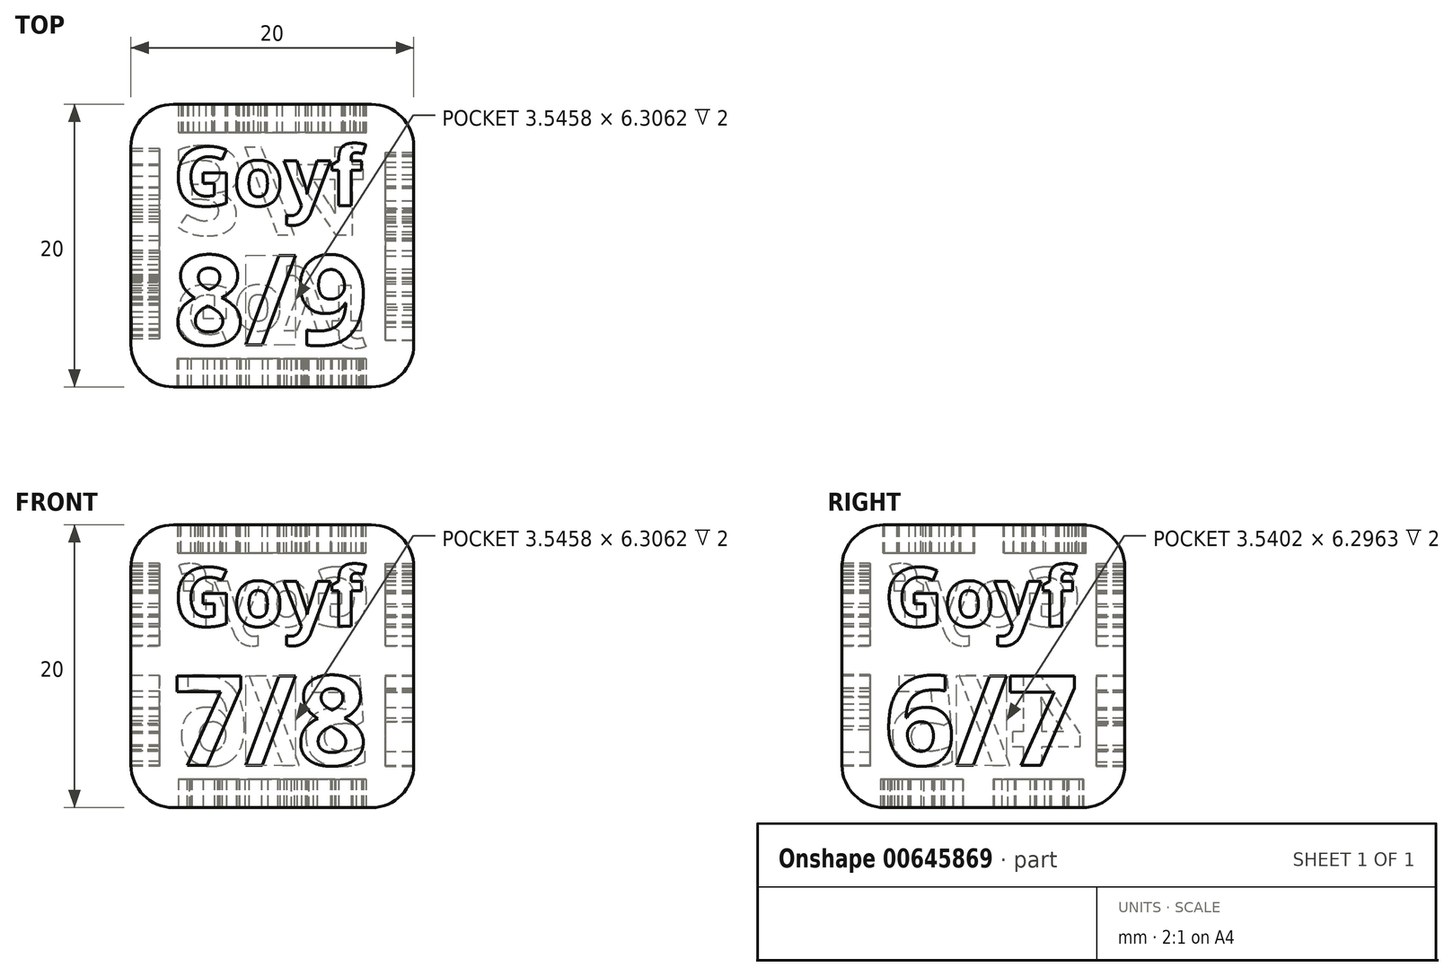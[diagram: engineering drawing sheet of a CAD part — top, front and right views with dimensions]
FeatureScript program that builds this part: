
annotation { "Feature Type Name" : "Feature", "Feature Type Description" : "" }
export const myFeature = defineFeature(function(context is Context, id is Id, definition is map)
    precondition{}
    {
        {
            var Q0;
            Q0=qCreatedBy(makeId("Top.planeOp"),FACE);
            var sketch = newSketch(context, id + "F0", { "sketchPlane" : qUnion([Q0])});
            skLineSegment(sketch, "E0.bottom", {"start": v(0, 0) * mm, "end": v(20, 0) * mm});
            skLineSegment(sketch, "E0.top", {"start": v(0, 20) * mm, "end": v(20, 20) * mm});
            skLineSegment(sketch, "E0.left", {"start": v(0, 0) * mm, "end": v(0, 20) * mm});
            skLineSegment(sketch, "E0.right", {"start": v(20, 0) * mm, "end": v(20, 20) * mm});
            skSolve(sketch);
        }
        {
            var Q0;
            Q0 = qSketchRegion(id + "F0", true);
            extrude(context, id + "F1", {"entities" : qUnion([Q0]), "depth" : 20 * mm, "offsetDistance" : 25 * mm});
        }
        {
            var Q0;
            Q0=makeQuery(id+"F1.opExtrude","CAP_EDGE",EDGE,{"disambiguationData":[OSD([sQuery(id+"F0.wireOp",EDGE,"E0.top")])],"isStart":true});
            var Q1;
            Q1=makeQuery(id+"F1.opExtrude","CAP_EDGE",EDGE,{"disambiguationData":[OSD([sQuery(id+"F0.wireOp",EDGE,"E0.left")])],"isStart":true});
            var Q2;
            Q2=makeQuery(id+"F1.opExtrude","SWEPT_EDGE",EDGE,{"disambiguationData":[OSD([sQuery(id+"F0.wireOp",EDGE,"E0.top"),sQuery(id+"F0.wireOp",EDGE,"E0.left")])]});
            var Q3;
            Q3=makeQuery(id+"F1.opExtrude","SWEPT_EDGE",EDGE,{"disambiguationData":[OSD([sQuery(id+"F0.wireOp",EDGE,"E0.top"),sQuery(id+"F0.wireOp",EDGE,"E0.right")])]});
            var Q4;
            Q4=makeQuery(id+"F1.opExtrude","SWEPT_FACE",FACE,{"disambiguationData":[OSD([sQuery(id+"F0.wireOp",EDGE,"E0.top")])]});
            var Q5;
            Q5=makeQuery(id+"F1.opExtrude","CAP_EDGE",EDGE,{"disambiguationData":[OSD([sQuery(id+"F0.wireOp",EDGE,"E0.right")])],"isStart":false});
            var Q6;
            Q6=makeQuery(id+"F1.opExtrude","CAP_EDGE",EDGE,{"disambiguationData":[OSD([sQuery(id+"F0.wireOp",EDGE,"E0.left")])],"isStart":false});
            var Q7;
            Q7=makeQuery(id+"F1.opExtrude","CAP_EDGE",EDGE,{"disambiguationData":[OSD([sQuery(id+"F0.wireOp",EDGE,"E0.bottom")])],"isStart":false});
            var Q8;
            Q8=makeQuery(id+"F1.opExtrude","SWEPT_EDGE",EDGE,{"disambiguationData":[OSD([sQuery(id+"F0.wireOp",EDGE,"E0.bottom"),sQuery(id+"F0.wireOp",EDGE,"E0.left")])]});
            var Q9;
            Q9=makeQuery(id+"F1.opExtrude","CAP_EDGE",EDGE,{"disambiguationData":[OSD([sQuery(id+"F0.wireOp",EDGE,"E0.bottom")])],"isStart":true});
            var Q10;
            Q10=makeQuery(id+"F1.opExtrude","SWEPT_EDGE",EDGE,{"disambiguationData":[OSD([sQuery(id+"F0.wireOp",EDGE,"E0.bottom"),sQuery(id+"F0.wireOp",EDGE,"E0.right")])]});
            var Q11;
            Q11=makeQuery(id+"F1.opExtrude","CAP_EDGE",EDGE,{"disambiguationData":[OSD([sQuery(id+"F0.wireOp",EDGE,"E0.right")])],"isStart":true});
            fillet(context, id + "F2", {"entities" : qUnion([Q0, Q1, Q2, Q3, Q4, Q5, Q6, Q7, Q8, Q9, Q10, Q11]), "radius" : 3 * mm, "tangentPropagation" : true, "allowEdgeOverflow" : false});
        }
        {
            var Q0;
            Q0=makeQuery(id+"F1.opExtrude","CAP_FACE",FACE,{"disambiguationData":[OSD([sQuery(id+"F0.wireOp",EDGE,"E0.bottom"),sQuery(id+"F0.wireOp",EDGE,"E0.top"),sQuery(id+"F0.wireOp",EDGE,"E0.left"),sQuery(id+"F0.wireOp",EDGE,"E0.right")])],"isStart":false});
            var sketch = newSketch(context, id + "F3", { "sketchPlane" : qUnion([Q0])});
            skText(sketch, "E1", { "text": "Goyf", "fontName": "OpenSans-Bold.ttf"});
            skText(sketch, "E2", { "text": "8/9", "fontName": "OpenSans-Bold.ttf"});
            const initialGuessF3  = {"E1": [0.003, 0.01282, 1, 0, 0.00418], "E2": [0.003, 0.003, 1, 0, 0.00636]};
            skSetInitialGuess(sketch, initialGuessF3);
            skSolve(sketch);
        }
        {
            var Q0;
            Q0=makeQuery(id+"F1.opExtrude","SWEPT_FACE",FACE,{"disambiguationData":[OSD([sQuery(id+"F0.wireOp",EDGE,"E0.bottom")])]});
            var sketch = newSketch(context, id + "F4", { "sketchPlane" : qUnion([Q0])});
            skText(sketch, "E3", { "text": "Goyf", "fontName": "OpenSans-Bold.ttf"});
            skText(sketch, "E4", { "text": "7/8", "fontName": "OpenSans-Bold.ttf"});
            const initialGuessF4  = {"E3": [0.003, 0.01282, 1, 0, 0.00418], "E4": [0.003, 0.003, 1, 0, 0.00636]};
            skSetInitialGuess(sketch, initialGuessF4);
            skSolve(sketch);
        }
        {
            var Q0;
            Q0=makeQuery(id+"F1.opExtrude","SWEPT_FACE",FACE,{"disambiguationData":[OSD([sQuery(id+"F0.wireOp",EDGE,"E0.right")])]});
            var sketch = newSketch(context, id + "F5", { "sketchPlane" : qUnion([Q0])});
            skText(sketch, "E5", { "text": "Goyf", "fontName": "OpenSans-Bold.ttf"});
            skText(sketch, "E6", { "text": "6/7", "fontName": "OpenSans-Bold.ttf"});
            const initialGuessF5  = {"E5": [0.003, 0.01282, 1, 0, 0.00418], "E6": [0.003, 0.003, 1, 0, 0.00635]};
            skSetInitialGuess(sketch, initialGuessF5);
            skSolve(sketch);
        }
        {
            var Q0;
            Q0=makeQuery(id+"F1.opExtrude","SWEPT_FACE",FACE,{"disambiguationData":[OSD([sQuery(id+"F0.wireOp",EDGE,"E0.top")])]});
            var sketch = newSketch(context, id + "F6", { "sketchPlane" : qUnion([Q0])});
            skText(sketch, "E7", { "text": "Goyf", "fontName": "OpenSans-Bold.ttf"});
            skText(sketch, "E8", { "text": "5/6", "fontName": "OpenSans-Bold.ttf"});
            const initialGuessF6  = {"E7": [-0.017, 0.01282, 1, 0, 0.00418], "E8": [-0.017, 0.003, 1, 0, 0.00635]};
            skSetInitialGuess(sketch, initialGuessF6);
            skSolve(sketch);
        }
        {
            var Q0;
            Q0=makeQuery(id+"F1.opExtrude","SWEPT_FACE",FACE,{"disambiguationData":[OSD([sQuery(id+"F0.wireOp",EDGE,"E0.left")])]});
            var sketch = newSketch(context, id + "F7", { "sketchPlane" : qUnion([Q0])});
            skText(sketch, "E9", { "text": "Goyf", "fontName": "OpenSans-Bold.ttf"});
            skText(sketch, "E10", { "text": "4/5", "fontName": "OpenSans-Bold.ttf"});
            const initialGuessF7  = {"E9": [-0.017, 0.01282, 1, 0, 0.00418], "E10": [-0.017, 0.003, 1, 0, 0.0064]};
            skSetInitialGuess(sketch, initialGuessF7);
            skSolve(sketch);
        }
        {
            var Q0;
            Q0=makeQuery(id+"F1.opExtrude","CAP_FACE",FACE,{"disambiguationData":[OSD([sQuery(id+"F0.wireOp",EDGE,"E0.bottom"),sQuery(id+"F0.wireOp",EDGE,"E0.top"),sQuery(id+"F0.wireOp",EDGE,"E0.left"),sQuery(id+"F0.wireOp",EDGE,"E0.right")])],"isStart":true});
            var sketch = newSketch(context, id + "F8", { "sketchPlane" : qUnion([Q0])});
            skText(sketch, "E11", { "text": "Goyf", "fontName": "OpenSans-Bold.ttf"});
            skText(sketch, "E12", { "text": "3/4", "fontName": "OpenSans-Bold.ttf"});
            const initialGuessF8  = {"E11": [0.003, -0.00718, 1, 0, 0.00418], "E12": [0.003, -0.017, 1, 0, 0.00628]};
            skSetInitialGuess(sketch, initialGuessF8);
            skSolve(sketch);
        }
        {
            var Q0;
            Q0 = qSketchRegion(id + "F3", true);
            extrude(context, id + "F9", {"entities" : qUnion([Q0]), "operationType" : NewBodyOperationType.REMOVE, "oppositeDirection" : true, "depth" : 2 * mm, "offsetDistance" : 25 * mm});
        }
        {
            var Q0;
            Q0 = qSketchRegion(id + "F4", true);
            extrude(context, id + "F10", {"entities" : qUnion([Q0]), "operationType" : NewBodyOperationType.REMOVE, "oppositeDirection" : true, "depth" : 2 * mm, "offsetDistance" : 25 * mm});
        }
        {
            var Q0;
            Q0 = qSketchRegion(id + "F5", true);
            extrude(context, id + "F11", {"entities" : qUnion([Q0]), "operationType" : NewBodyOperationType.REMOVE, "oppositeDirection" : true, "depth" : 2 * mm, "offsetDistance" : 25 * mm});
        }
        {
            var Q0;
            Q0 = qSketchRegion(id + "F6", true);
            extrude(context, id + "F12", {"entities" : qUnion([Q0]), "operationType" : NewBodyOperationType.REMOVE, "oppositeDirection" : true, "depth" : 2 * mm, "offsetDistance" : 25 * mm});
        }
        {
            var Q0;
            Q0 = qSketchRegion(id + "F7", true);
            extrude(context, id + "F13", {"entities" : qUnion([Q0]), "operationType" : NewBodyOperationType.REMOVE, "oppositeDirection" : true, "depth" : 2 * mm, "offsetDistance" : 25 * mm});
        }
        {
            var Q0;
            Q0 = qSketchRegion(id + "F8", true);
            extrude(context, id + "F14", {"entities" : qUnion([Q0]), "operationType" : NewBodyOperationType.REMOVE, "oppositeDirection" : true, "depth" : 2 * mm, "offsetDistance" : 25 * mm});
        }
    });
